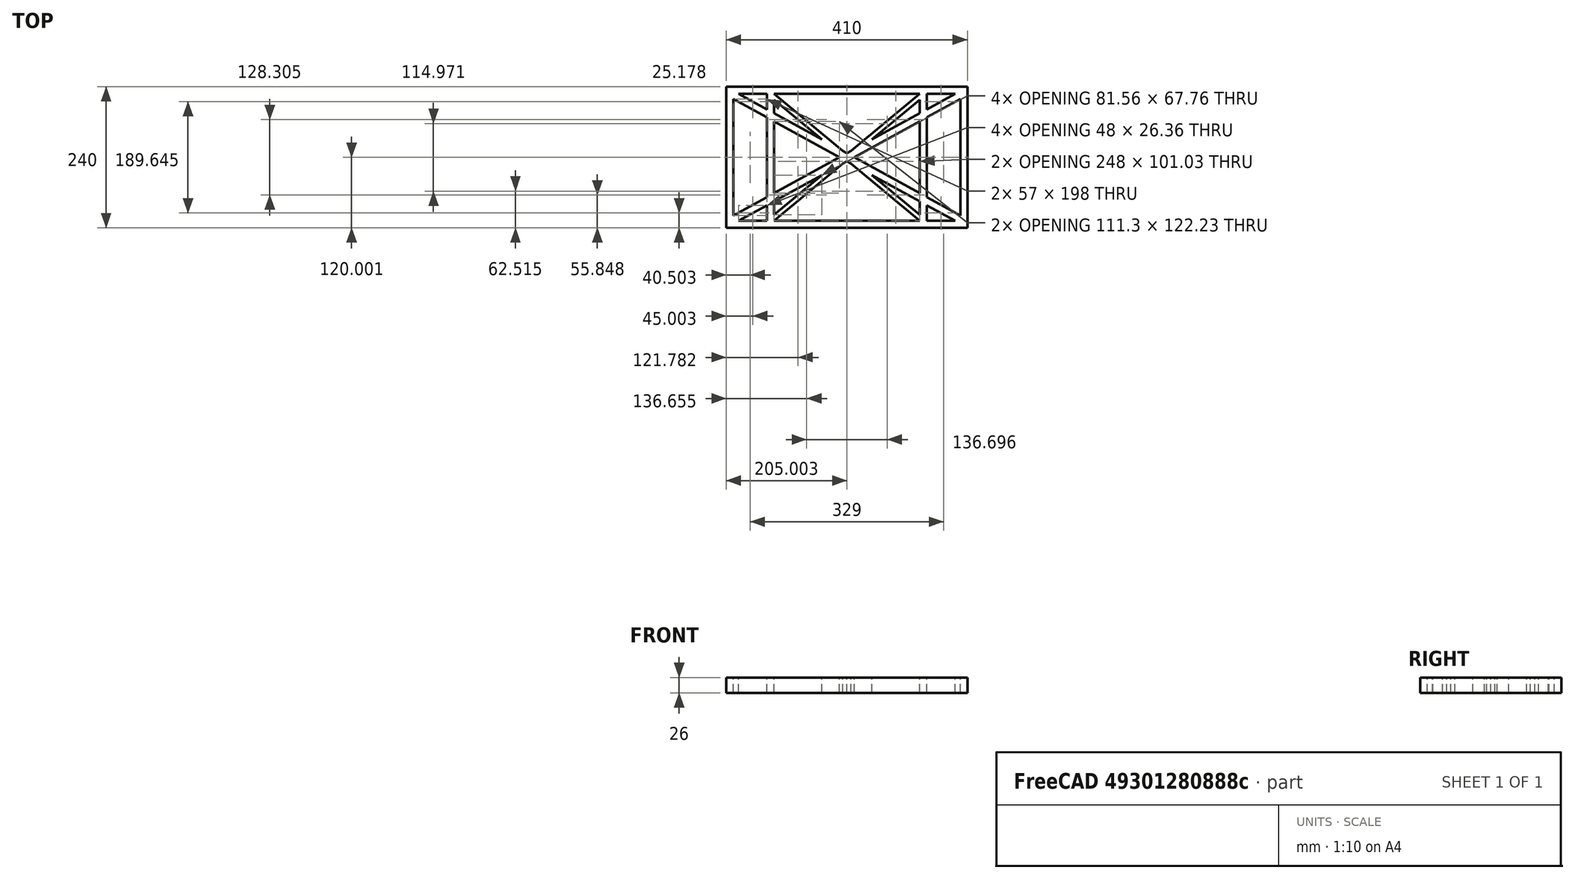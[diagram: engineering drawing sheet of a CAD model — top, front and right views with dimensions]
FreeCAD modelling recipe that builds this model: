
FCSTD DOCUMENT  (FreeCAD 0.19R0.19.2)
Label: laptopStand020
License: All rights reserved
LicenseURL: http://en.wikipedia.org/wiki/All_rights_reserved
objects: Sketcher::SketchObject×3, Part::Extrusion×1
note: 4 computed .brp shape members not serialized (recipe doc carries the construction recipe); baked Part::Feature solids carry a one-line shape summary decoded from their .brp

FEATURE [Sketcher::SketchObject] Sketch
  FullyConstrained = true
  sketch-geometry (52):
    g0: LineSegment StartX=-22.9272 StartY=136.221 StartZ=0 EndX=-22.9272 EndY=-103.779 EndZ=0
    g1: LineSegment StartX=-22.9272 StartY=136.221 StartZ=0 EndX=387.073 EndY=136.221 EndZ=0
    g2: LineSegment StartX=-22.9272 StartY=-103.779 StartZ=0 EndX=387.073 EndY=-103.779 EndZ=0
    g3: LineSegment StartX=387.073 StartY=136.221 StartZ=0 EndX=387.073 EndY=-103.779 EndZ=0
    g4: LineSegment StartX=375.073 StartY=115.221 StartZ=0 EndX=318.073 EndY=83.9235 EndZ=0
    g5: LineSegment StartX=-10.9272 StartY=-82.7794 StartZ=0 EndX=46.0728 EndY=-51.4823 EndZ=0
    g6: LineSegment StartX=-1.92719 StartY=124.221 StartZ=0 EndX=46.0728 EndY=97.8651 EndZ=0
    g7: LineSegment StartX=366.073 StartY=-91.7794 StartZ=0 EndX=318.073 EndY=-65.424 EndZ=0
    g8: LineSegment StartX=-10.9272 StartY=115.221 StartZ=0 EndX=-10.9272 EndY=-82.7794 EndZ=0
    g9: LineSegment StartX=375.073 StartY=-82.7794 StartZ=0 EndX=375.073 EndY=115.221 EndZ=0
    g10: LineSegment StartX=-1.92719 StartY=-91.7794 StartZ=0 EndX=46.0728 EndY=-91.7794 EndZ=0
    g11: LineSegment StartX=318.073 StartY=124.221 StartZ=0 EndX=366.073 EndY=124.221 EndZ=0
    g12: LineSegment StartX=306.073 StartY=-81.8102 StartZ=0 EndX=224.513 EndY=-14.0532 EndZ=0
    g13: LineSegment StartX=58.0728 StartY=114.251 StartZ=0 EndX=139.632 EndY=46.4944 EndZ=0
    g14: LineSegment StartX=306.073 StartY=124.221 StartZ=0 EndX=189.124 EndY=27.0628 EndZ=0
    g15: LineSegment StartX=58.0728 StartY=-91.7794 StartZ=0 EndX=175.022 EndY=5.37834 EndZ=0
    g16: LineSegment StartX=46.0728 StartY=124.221 StartZ=0 EndX=46.0728 EndY=97.8651 EndZ=0
    g17: LineSegment StartX=58.0728 StartY=-81.8102 StartZ=0 EndX=58.0728 EndY=-58.8351 EndZ=0
    g18: LineSegment StartX=318.073 StartY=124.221 StartZ=0 EndX=318.073 EndY=97.8651 EndZ=0
    g19: LineSegment StartX=306.073 StartY=114.251 StartZ=0 EndX=306.073 EndY=91.2763 EndZ=0
    g20: LineSegment StartX=182.073 StartY=23.1914 StartZ=0 EndX=189.124 EndY=27.0628 EndZ=0
    g21: LineSegment StartX=182.073 StartY=9.24976 StartZ=0 EndX=175.022 EndY=5.37834 EndZ=0
    g22: LineSegment StartX=224.513 StartY=46.4944 StartZ=0 EndX=306.073 EndY=114.251 EndZ=0
    g23: LineSegment StartX=175.022 StartY=27.0628 StartZ=0 EndX=58.0728 EndY=124.221 EndZ=0
    g24: LineSegment StartX=169.377 StartY=16.2206 StartZ=0 EndX=58.0728 EndY=77.3346 EndZ=0
    g25: LineSegment StartX=139.632 StartY=-14.0532 StartZ=0 EndX=58.0728 EndY=-81.8102 EndZ=0
    g26: LineSegment StartX=194.768 StartY=16.2206 StartZ=0 EndX=306.073 EndY=-44.8935 EndZ=0
    g27: LineSegment StartX=224.513 StartY=46.4944 StartZ=0 EndX=306.073 EndY=91.2763 EndZ=0
    g28: LineSegment StartX=175.022 StartY=27.0628 StartZ=0 EndX=182.073 EndY=23.1914 EndZ=0
    g29: LineSegment StartX=139.632 StartY=-14.0532 StartZ=0 EndX=58.0728 EndY=-58.8351 EndZ=0
    g30: LineSegment StartX=189.124 StartY=5.37834 StartZ=0 EndX=182.073 EndY=9.24976 EndZ=0
    g31: LineSegment StartX=189.124 StartY=5.37834 StartZ=0 EndX=306.073 EndY=-91.7794 EndZ=0
    g32: LineSegment StartX=306.073 StartY=77.3346 StartZ=0 EndX=306.073 EndY=-44.8935 EndZ=0
    g33: LineSegment StartX=318.073 StartY=83.9235 StartZ=0 EndX=318.073 EndY=-51.4823 EndZ=0
    g34: LineSegment StartX=318.073 StartY=97.8651 StartZ=0 EndX=366.073 EndY=124.221 EndZ=0
    g35: LineSegment StartX=306.073 StartY=77.3346 StartZ=0 EndX=194.768 EndY=16.2206 EndZ=0
    g36: LineSegment StartX=306.073 StartY=-58.8351 StartZ=0 EndX=224.513 EndY=-14.0532 EndZ=0
    g37: LineSegment StartX=306.073 StartY=-58.8351 StartZ=0 EndX=306.073 EndY=-81.8102 EndZ=0
    g38: LineSegment StartX=318.073 StartY=-51.4823 StartZ=0 EndX=375.073 EndY=-82.7794 EndZ=0
    g39: LineSegment StartX=318.073 StartY=-65.424 StartZ=0 EndX=318.073 EndY=-91.7794 EndZ=0
    g40: LineSegment StartX=306.073 StartY=124.221 StartZ=0 EndX=58.0728 EndY=124.221 EndZ=0
    g41: LineSegment StartX=318.073 StartY=-91.7794 StartZ=0 EndX=366.073 EndY=-91.7794 EndZ=0
    g42: LineSegment StartX=58.0728 StartY=-91.7794 StartZ=0 EndX=306.073 EndY=-91.7794 EndZ=0
    g43: LineSegment StartX=58.0728 StartY=-44.8935 StartZ=0 EndX=58.0728 EndY=77.3346 EndZ=0
    g44: LineSegment StartX=46.0728 StartY=-65.424 StartZ=0 EndX=-1.92719 EndY=-91.7794 EndZ=0
    g45: LineSegment StartX=46.0728 StartY=-65.424 StartZ=0 EndX=46.0728 EndY=-91.7794 EndZ=0
    g46: LineSegment StartX=58.0728 StartY=-44.8935 StartZ=0 EndX=169.377 EndY=16.2206 EndZ=0
    g47: LineSegment StartX=58.0728 StartY=91.2763 StartZ=0 EndX=58.0728 EndY=114.251 EndZ=0
    g48: LineSegment StartX=46.0728 StartY=83.9235 StartZ=0 EndX=46.0728 EndY=-51.4823 EndZ=0
    g49: LineSegment StartX=46.0728 StartY=124.221 StartZ=0 EndX=-1.92719 EndY=124.221 EndZ=0
    g50: LineSegment StartX=58.0728 StartY=91.2763 StartZ=0 EndX=139.632 EndY=46.4944 EndZ=0
    g51: LineSegment StartX=46.0728 StartY=83.9235 StartZ=0 EndX=-10.9272 EndY=115.221 EndZ=0
  constraints (102):
    c: Vertical(g0)
    c: Distance(g0) = 240
    c: Horizontal(g1)
    c: Distance(g1) = 410
    c: Coincident(g1,g0)
    c: Coincident(g2,g0)
    c: Horizontal(g2)
    c: Coincident(g3,g1)
    c: Vertical(g3)
    c: Coincident(g2,g3)
    c: Block(g1)
    c: Horizontal(g10)
    c: Horizontal(g11)
    c: PointOnObject(g35,g6)
    c: Coincident(g28,g20)
    c: Coincident(g30,g21)
    c: Tangent(g7,g24)
    c: PointOnObject(g24,g5)
    c: PointOnObject(g26,g4)
    c: Coincident(g20,g14)
    c: Tangent(g20,g27)
    c: Coincident(g50,g13)
    c: Coincident(g28,g23)
    c: Coincident(g22,g27)
    c: Coincident(g21,g15)
    c: Coincident(g29,g25)
    c: Tangent(g21,g29)
    c: Coincident(g36,g12)
    c: Coincident(g31,g30)
    c: Coincident(g22,g19)
    c: Tangent(g19,g32)
    c: Tangent(g18,g33)
    c: Coincident(g27,g19)
    c: Tangent(g27,g34)
    c: Coincident(g4,g33)
    c: Coincident(g35,g32)
    c: Tangent(g4,g35)
    c: Coincident(g37,g12)
    c: Tangent(g7,g36)
    c: Tangent(g32,g37)
    c: Coincident(g26,g32)
    c: Tangent(g26,g38)
    c: Coincident(g33,g38)
    c: Coincident(g39,g7)
    c: Tangent(g33,g39)
    c: Coincident(g25,g17)
    c: Tangent(g17,g43)
    c: Coincident(g29,g17)
    c: Tangent(g29,g44)
    c: Coincident(g45,g44)
    c: Tangent(g16,g45)
    c: Coincident(g5,g48)
    c: Coincident(g46,g43)
    c: Tangent(g5,g46)
    c: Tangent(g43,g47)
    c: Tangent(g16,g48)
    c: Coincident(g13,g47)
    c: PointOnObject(g40,g23)
    c: Tangent(g40,g49)
    c: Coincident(g6,g16)
    c: Coincident(g50,g47)
    c: Tangent(g6,g50)
    c: Coincident(g24,g43)
    c: Coincident(g51,g48)
    c: Tangent(g24,g51)
    c: Block(g23)
    c: Block(g14)
    c: Block(g20)
    c: Block(g40)
    c: Block(g18)
    c: Block(g34)
    c: Block(g4)
    c: Block(g38)
    c: Block(g9)
    c: Block(g36)
    c: Block(g37)
    c: Block(g7)
    c: Block(g39)
    c: Block(g22)
    c: Block(g31)
    c: Block(g42)
    c: Block(g21)
    c: Block(g15)
    c: Block(g29)
    c: Block(g25)
    c: Block(g45)
    c: Block(g44)
    c: Block(g5)
    c: Block(g8)
    c: Block(g51)
    c: Block(g6)
    c: Block(g16)
    c: Block(g13)
    c: Block(g47)
    c: Block(g35)
    c: Block(g32)
    c: Block(g24)
    c: Block(g46)
    c: Block(g49)
    c: Block(g11)
    c: Block(g41)
    c: Block(g10)
FEATURE [Part::Extrusion] Extrude
  Base = -> Sketch
  Dir = (0,0,1)
  DirMode = 2
  FaceMakerClass = Part::FaceMakerBullseye
  LengthFwd = 26
  LengthRev = 0
  Solid = true
  Symmetric = false
FEATURE [Sketcher::SketchObject] Sketch001
  FullyConstrained = true
  MapMode = 4
  Placement = pos=(0,0,0) rot=(0.57735,0.57735,0.57735;2.0944rad)
  Support = -> [Sketch]
  sketch-geometry (9):
    g0: LineSegment StartX=17.2228 StartY=-16.0875 StartZ=0 EndX=117.223 EndY=-16.0875 EndZ=0
    g1: LineSegment StartX=17.2228 StartY=-16.0875 StartZ=0 EndX=17.2228 EndY=-19.0875 EndZ=0
    g2: LineSegment StartX=117.223 StartY=-16.0875 StartZ=0 EndX=117.223 EndY=-19.0875 EndZ=0
    g3: BSplineCurve PolesCount=3 KnotsCount=2 Degree=2 IsPeriodic=0
    g4: LineSegment StartX=94.6577 StartY=-26.1351 StartZ=0 EndX=24.2583 EndY=-213.335 EndZ=0
    g5: LineSegment StartX=-9.4377 StartY=-200.664 StartZ=0 EndX=24.2583 EndY=-213.335 EndZ=0
    g6: LineSegment StartX=-9.4377 StartY=-200.664 StartZ=0 EndX=56.1962 EndY=-26.1351 EndZ=0
    g7: LineSegment StartX=17.2228 StartY=-19.0875 StartZ=0 EndX=38.8094 EndY=-19.0875 EndZ=0
    g8: BSplineCurve PolesCount=4 KnotsCount=2 Degree=3 IsPeriodic=0
  constraints (24):
    c: Horizontal(g0)
    c: Distance(g0) = 100
    c: Block(g0)
    c: Coincident(g1,g0)
    c: Vertical(g1)
    c: Distance(g1) = 3
    c: Coincident(g2,g0)
    c: Vertical(g2)
    c: Distance(g2) = 3
    c: Block(g3)
    c: Coincident(g3,g2)
    c: Coincident(g4,g3)
    c: Block(g4)
    c: Distance(g5) = 36
    c: Perpendicular(g5,g4)
    c: Coincident(g5,g4)
    c: Parallel(g4,g6)
    c: Coincident(g6,g5)
    c: Coincident(g7,g1)
    c: Horizontal(g7)
    c: Block(g8)
    c: Coincident(g8,g7)
    c: Coincident(g8,g6)
    c: Block(g6)
FEATURE [Sketcher::SketchObject] Sketch002
  FullyConstrained = true
  Placement = pos=(0,0,0) rot=(-1,0,0;4.71239rad)
